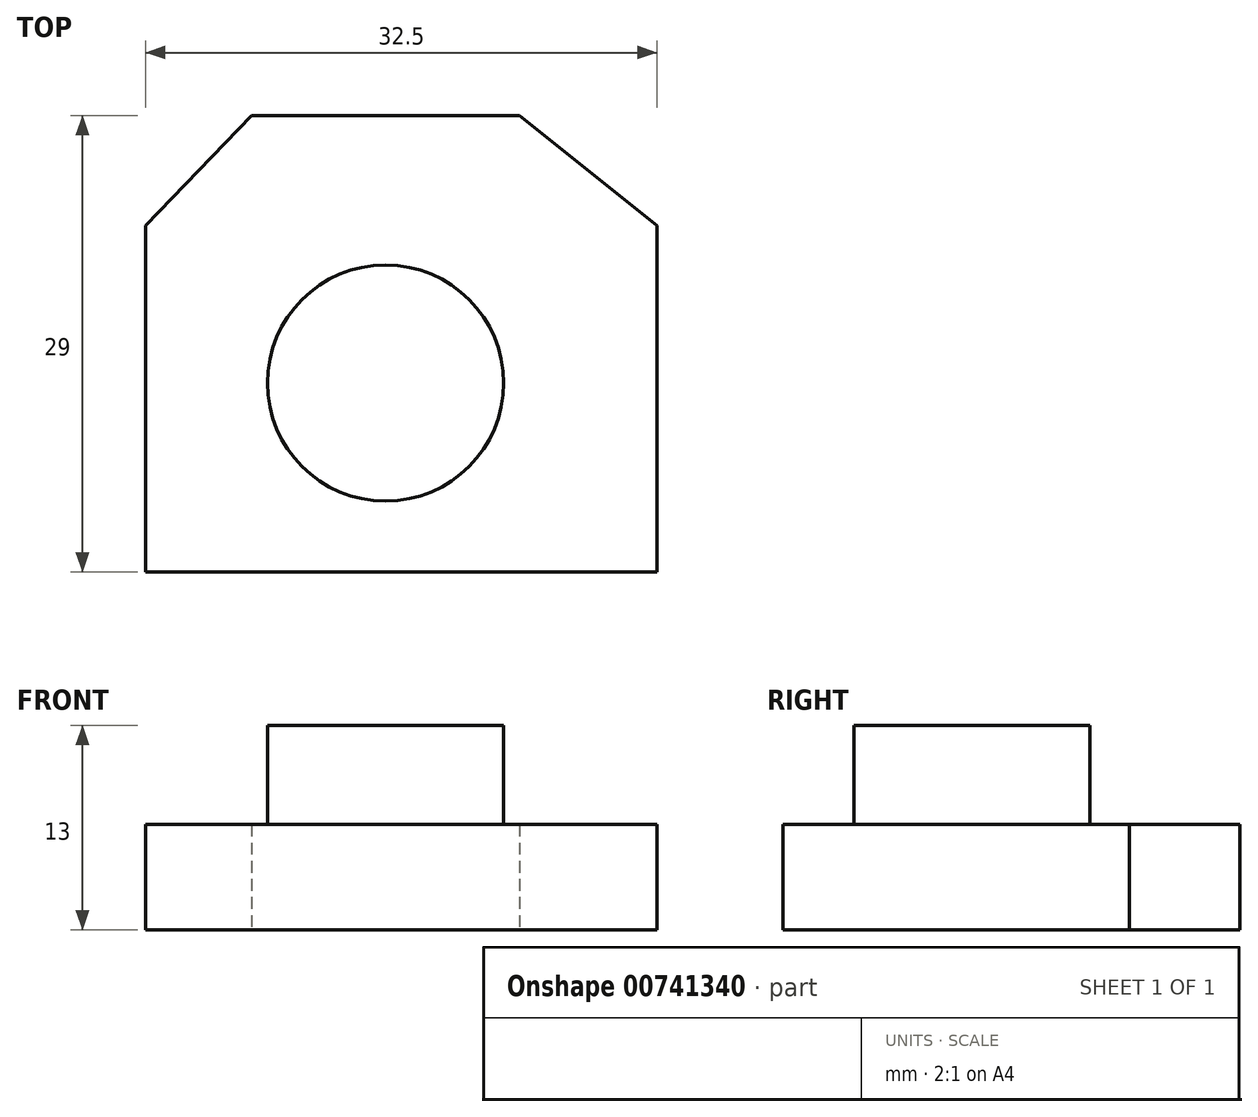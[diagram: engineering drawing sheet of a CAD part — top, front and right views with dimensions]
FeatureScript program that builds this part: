
annotation { "Feature Type Name" : "Feature", "Feature Type Description" : "" }
export const myFeature = defineFeature(function(context is Context, id is Id, definition is map)
    precondition{}
    {
        {
            var Q0;
            Q0=qCreatedBy(makeId("Top.planeOp"),FACE);
            var sketch = newSketch(context, id + "F0", { "sketchPlane" : qUnion([Q0])});
            skLineSegment(sketch, "E0.bottom", {"start": v(-15.25, 10) * mm, "end": v(17.25, 10) * mm});
            skLineSegment(sketch, "E0.top", {"start": v(-15.25, -12) * mm, "end": v(17.25, -12) * mm});
            skLineSegment(sketch, "E0.left", {"start": v(-15.25, 10) * mm, "end": v(-15.25, -12) * mm});
            skLineSegment(sketch, "E0.right", {"start": v(17.25, 10) * mm, "end": v(17.25, -12) * mm});
            skLineSegment(sketch, "E1", {"start": v(-15.25, 10) * mm, "end": v(-8.5, 17) * mm});
            skLineSegment(sketch, "E2", {"start": v(-8.5, 17) * mm, "end": v(8.5, 17) * mm});
            skLineSegment(sketch, "E3", {"start": v(8.5, 17) * mm, "end": v(17.25, 10) * mm});
            skSolve(sketch);
        }
        {
            var Q0;
            Q0=makeQuery(id+"F0.imprint","IMPRINT",FACE,{"disambiguationData":[TD([[makeQuery(id+"F0.imprint","IMPRINT",EDGE,{"derivedFrom":sQuery(id+"F0.wireOp",EDGE,"E0.bottom")}),-1.0]])]});
            var Q1;
            Q1=makeQuery(id+"F0.imprint","IMPRINT",FACE,{"disambiguationData":[TD([[makeQuery(id+"F0.imprint","IMPRINT",EDGE,{"derivedFrom":sQuery(id+"F0.wireOp",EDGE,"E0.bottom")}),1.0]])]});
            extrude(context, id + "F1", {"entities" : qUnion([Q0, Q1]), "depth" : 6.7 * mm, "offsetDistance" : 25 * mm});
        }
        {
            var Q0;
            Q0=qCreatedBy(makeId("Top.planeOp"),FACE);
            var sketch = newSketch(context, id + "F2", { "sketchPlane" : qUnion([Q0])});
            skCircle(sketch, "E4", {"center": v(0, 0) * mm, "radius": 7.5 * mm});
            skSolve(sketch);
        }
        {
            var Q0;
            Q0 = qSketchRegion(id + "F2", true);
            extrude(context, id + "F3", {"entities" : qUnion([Q0]), "operationType" : NewBodyOperationType.ADD, "depth" : 13 * mm, "offsetDistance" : 25 * mm});
        }
    });
